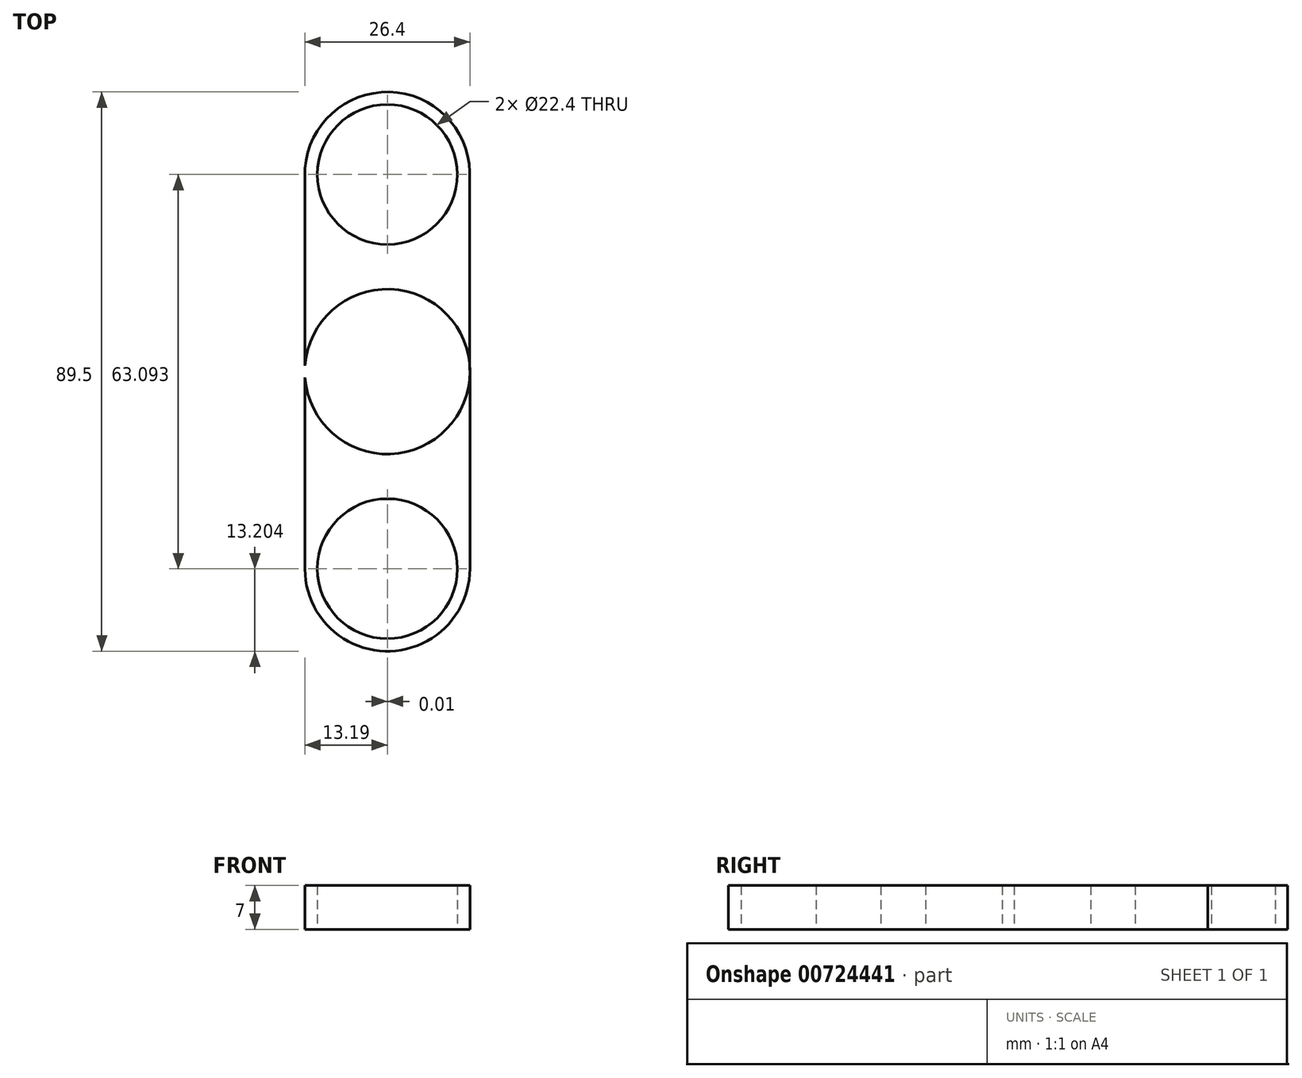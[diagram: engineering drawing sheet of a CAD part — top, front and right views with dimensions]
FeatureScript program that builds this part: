
annotation { "Feature Type Name" : "Feature", "Feature Type Description" : "" }
export const myFeature = defineFeature(function(context is Context, id is Id, definition is map)
    precondition{}
    {
        {
            var Q0;
            Q0=qCreatedBy(makeId("Top.planeOp"),FACE);
            var sketch = newSketch(context, id + "F0", { "sketchPlane" : qUnion([Q0])});
            skCircle(sketch, "E0", {"center": v(0, 0) * mm, "radius": 11.2 * mm});
            skCircle(sketch, "E1", {"center": v(0, 0) * mm, "radius": 13.2 * mm});
            skCircle(sketch, "E2", {"center": v(0, 31.55) * mm, "radius": 11.2 * mm});
            skArc(sketch, "E3", {"start": v(13.2, 31.17) * mm, "mid": v(-0.29, 44.74) * mm, "end": v(-13.17, 30.6) * mm});
            skArc(sketch, "E4.1.0", {"start": v(-13.17, -30.75) * mm, "mid": v(-0.39, -44.74) * mm, "end": v(13.21, -31.54) * mm});
            skCircle(sketch, "E4.1.1", {"center": v(0.01, -31.55) * mm, "radius": 11.2 * mm});
            skLineSegment(sketch, "E5", {"start": v(-13.17, 32.5) * mm, "end": v(-13.17, -30.75) * mm});
            skLineSegment(sketch, "E6", {"start": v(13.2, 31.94) * mm, "end": v(13.21, -31.54) * mm});
            skSolve(sketch);
        }
        {
            var Q0;
            Q0=makeQuery(id+"F0.imprint","IMPRINT",FACE,{"disambiguationData":[TD([[makeQuery(id+"F0.imprint","IMPRINT",EDGE,{"derivedFrom":sQuery(id+"F0.wireOp",EDGE,"E2")}),-1.0]])]});
            extrude(context, id + "F1", {"entities" : qUnion([Q0]), "depth" : 7 * mm, "offsetDistance" : 25 * mm});
        }
    });
